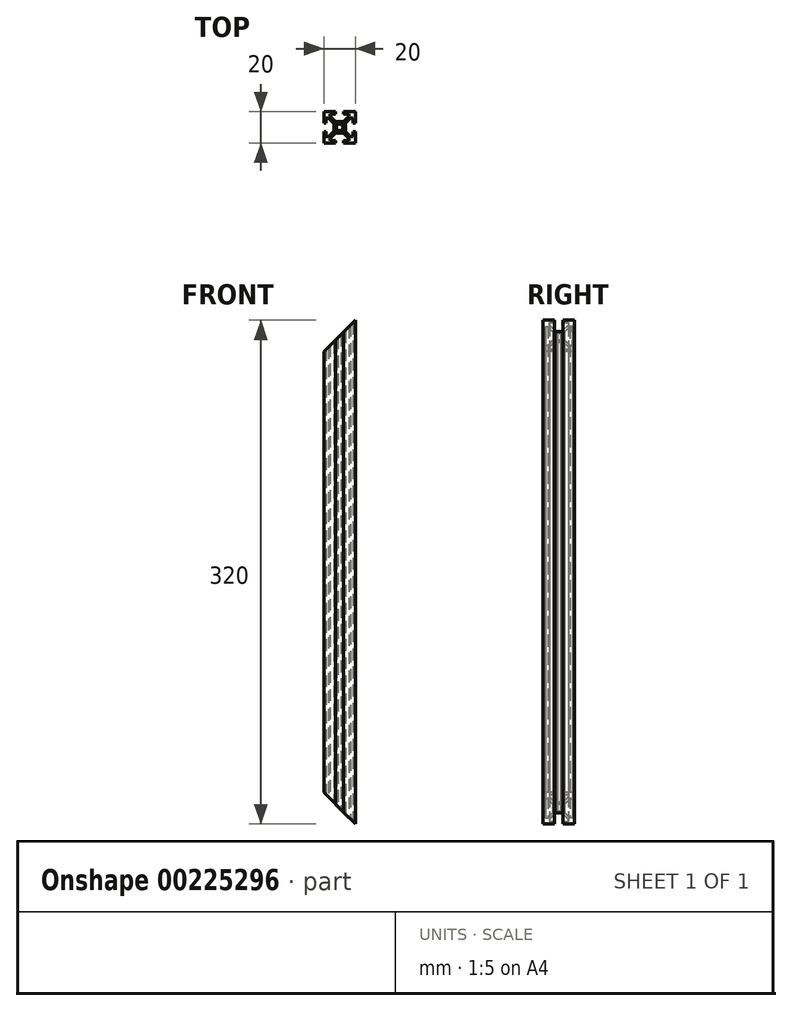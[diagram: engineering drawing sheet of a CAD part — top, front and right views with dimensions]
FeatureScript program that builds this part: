
annotation { "Feature Type Name" : "Feature", "Feature Type Description" : "" }
export const myFeature = defineFeature(function(context is Context, id is Id, definition is map)
    precondition{}
    {
        {
            var Q0;
            Q0=qCreatedBy(makeId("Top.planeOp"),FACE);
            var sketch = newSketch(context, id + "F0", { "sketchPlane" : qUnion([Q0])});
            skLineSegment(sketch, "E0.bottom", {"start": v(10, 10) * mm, "end": v(-10, 10) * mm});
            skLineSegment(sketch, "E0.top", {"start": v(10, -10) * mm, "end": v(-10, -10) * mm});
            skLineSegment(sketch, "E0.left", {"start": v(10, 10) * mm, "end": v(10, -10) * mm});
            skLineSegment(sketch, "E0.right", {"start": v(-10, 10) * mm, "end": v(-10, -10) * mm});
            skPoint(sketch, "E0.middle", {"position": v(0, 0) * mm});
            skLineSegment(sketch, "E1", {"start": v(-10, 10) * mm, "end": v(10, -10) * mm, "construction": true});
            skLineSegment(sketch, "E2", {"start": v(-10, -10) * mm, "end": v(10, 10) * mm, "construction": true});
            skLineSegment(sketch, "E3", {"start": v(0, 10) * mm, "end": v(0, -10) * mm, "construction": true});
            skLineSegment(sketch, "E4", {"start": v(-10, 0) * mm, "end": v(10, 0) * mm, "construction": true});
            skPoint(sketch, "E4.endSnap0", {"position": v(10, 0) * mm});
            skLineSegment(sketch, "E5", {"start": v(-2.63, 13.49) * mm, "end": v(2.63, 13.49) * mm});
            skLineSegment(sketch, "E6", {"start": v(2.63, 13.49) * mm, "end": v(2.63, 8.5) * mm});
            skLineSegment(sketch, "E7", {"start": v(2.63, 8.5) * mm, "end": v(6, 8.5) * mm});
            skLineSegment(sketch, "E8", {"start": v(6, 8.5) * mm, "end": v(6, 7.06) * mm});
            skLineSegment(sketch, "E9", {"start": v(6, 7.06) * mm, "end": v(2.6, 3.66) * mm});
            skLineSegment(sketch, "E10", {"start": v(2.6, 3.66) * mm, "end": v(-2.6, 3.66) * mm});
            skLineSegment(sketch, "E11", {"start": v(-2.6, 3.66) * mm, "end": v(-6, 7.06) * mm});
            skLineSegment(sketch, "E12", {"start": v(-6, 7.06) * mm, "end": v(-6, 8.5) * mm});
            skLineSegment(sketch, "E13", {"start": v(-6, 8.5) * mm, "end": v(-2.63, 8.5) * mm});
            skLineSegment(sketch, "E14", {"start": v(-2.63, 8.5) * mm, "end": v(-2.63, 13.49) * mm});
            skCircle(sketch, "E15", {"center": v(0, 0) * mm, "radius": 2.1 * mm});
            skLineSegment(sketch, "E16.MirrorCS", {"start": v(-7.06, 6) * mm, "end": v(-8.5, 6) * mm});
            skLineSegment(sketch, "E17.MirrorCS", {"start": v(-3.66, 2.6) * mm, "end": v(-7.06, 6) * mm});
            skLineSegment(sketch, "E18.MirrorCS", {"start": v(-8.5, 6) * mm, "end": v(-8.5, 2.63) * mm});
            skLineSegment(sketch, "E19.MirrorCS", {"start": v(-3.66, -2.6) * mm, "end": v(-3.66, 2.6) * mm});
            skLineSegment(sketch, "E20.MirrorCS", {"start": v(-7.06, -6) * mm, "end": v(-3.66, -2.6) * mm});
            skLineSegment(sketch, "E21.MirrorCS", {"start": v(-8.5, -6) * mm, "end": v(-7.06, -6) * mm});
            skLineSegment(sketch, "E22.MirrorCS", {"start": v(-8.5, -2.63) * mm, "end": v(-8.5, -6) * mm});
            skLineSegment(sketch, "E23.MirrorCS", {"start": v(-13.49, -2.63) * mm, "end": v(-8.5, -2.63) * mm});
            skLineSegment(sketch, "E24.MirrorCS", {"start": v(-13.49, 2.63) * mm, "end": v(-13.49, -2.63) * mm});
            skLineSegment(sketch, "E25.MirrorCS", {"start": v(-8.5, 2.63) * mm, "end": v(-13.49, 2.63) * mm});
            skLineSegment(sketch, "E26.MirrorCS", {"start": v(-2.6, -3.66) * mm, "end": v(-6, -7.06) * mm});
            skLineSegment(sketch, "E27.MirrorCS", {"start": v(2.6, -3.66) * mm, "end": v(-2.6, -3.66) * mm});
            skLineSegment(sketch, "E28.MirrorCS", {"start": v(6, -7.06) * mm, "end": v(2.6, -3.66) * mm});
            skLineSegment(sketch, "E29.MirrorCS", {"start": v(6, -8.5) * mm, "end": v(6, -7.06) * mm});
            skLineSegment(sketch, "E30.MirrorCS", {"start": v(2.63, -8.5) * mm, "end": v(6, -8.5) * mm});
            skLineSegment(sketch, "E31.MirrorCS", {"start": v(2.63, -13.49) * mm, "end": v(2.63, -8.5) * mm});
            skLineSegment(sketch, "E32.MirrorCS", {"start": v(-2.63, -13.49) * mm, "end": v(2.63, -13.49) * mm});
            skLineSegment(sketch, "E33.MirrorCS", {"start": v(-2.63, -8.5) * mm, "end": v(-2.63, -13.49) * mm});
            skLineSegment(sketch, "E34.MirrorCS", {"start": v(-6, -8.5) * mm, "end": v(-2.63, -8.5) * mm});
            skLineSegment(sketch, "E35.MirrorCS", {"start": v(-6, -7.06) * mm, "end": v(-6, -8.5) * mm});
            skLineSegment(sketch, "E36.MirrorCS", {"start": v(7.06, 6) * mm, "end": v(3.66, 2.6) * mm});
            skLineSegment(sketch, "E37.MirrorCS", {"start": v(8.5, 6) * mm, "end": v(7.06, 6) * mm});
            skLineSegment(sketch, "E38.MirrorCS", {"start": v(8.5, 2.63) * mm, "end": v(8.5, 6) * mm});
            skLineSegment(sketch, "E39.MirrorCS", {"start": v(13.49, 2.63) * mm, "end": v(8.5, 2.63) * mm});
            skLineSegment(sketch, "E40.MirrorCS", {"start": v(13.49, -2.63) * mm, "end": v(13.49, 2.63) * mm});
            skLineSegment(sketch, "E41.MirrorCS", {"start": v(8.5, -2.63) * mm, "end": v(13.49, -2.63) * mm});
            skLineSegment(sketch, "E42.MirrorCS", {"start": v(8.5, -6) * mm, "end": v(8.5, -2.63) * mm});
            skLineSegment(sketch, "E43.MirrorCS", {"start": v(7.06, -6) * mm, "end": v(8.5, -6) * mm});
            skLineSegment(sketch, "E44.MirrorCS", {"start": v(3.66, -2.6) * mm, "end": v(7.06, -6) * mm});
            skLineSegment(sketch, "E45.MirrorCS", {"start": v(3.66, 2.6) * mm, "end": v(3.66, -2.6) * mm});
            skCircle(sketch, "E46", {"center": v(-1.48, 1.48) * mm, "radius": 0.7 * mm});
            skCircle(sketch, "E47.MirrorC", {"center": v(1.48, 1.48) * mm, "radius": 0.7 * mm});
            skCircle(sketch, "E48.MirrorC", {"center": v(-1.48, -1.48) * mm, "radius": 0.7 * mm});
            skCircle(sketch, "E49.MirrorC", {"center": v(1.48, -1.48) * mm, "radius": 0.7 * mm});
            skSolve(sketch);
        }
        {
            var Q0;
            {var subQ29=sQuery(id+"F0.wireOp",EDGE,"E7");Q0=makeQuery(id+"F0.imprint","IMPRINT",FACE,{"disambiguationData":[TD([[makeQuery(id+"F0.imprint","IMPRINT",EDGE,{"derivedFrom":subQ29}),1.0]])]});}
            extrude(context, id + "F1", {"entities" : qUnion([Q0]), "depth" : 320 * mm});
        }
        {
            var Q0;
            Q0=qCreatedBy(makeId("Front.planeOp"),FACE);
            var sketch = newSketch(context, id + "F2", { "sketchPlane" : qUnion([Q0])});
            skLineSegment(sketch, "E50.0", {"start": v(10, 320) * mm, "end": v(10, 0) * mm});
            skLineSegment(sketch, "E51.0", {"start": v(-10, 320) * mm, "end": v(-10, 0) * mm});
            skLineSegment(sketch, "E52", {"start": v(10, 0) * mm, "end": v(-10, 20) * mm});
            skLineSegment(sketch, "E53.0", {"start": v(10, 0) * mm, "end": v(2.63, 0) * mm});
            skLineSegment(sketch, "E54", {"start": v(-10, 20) * mm, "end": v(-10, 0) * mm});
            skLineSegment(sketch, "E55", {"start": v(10, 0) * mm, "end": v(-10, 0) * mm});
            skLineSegment(sketch, "E56", {"start": v(-91.6, 160) * mm, "end": v(92.38, 160) * mm, "construction": true});
            skLineSegment(sketch, "E57.MirrorCS", {"start": v(10, 320) * mm, "end": v(-10, 300) * mm});
            skLineSegment(sketch, "E58.MirrorCS", {"start": v(-10, 300) * mm, "end": v(-10, 320) * mm});
            skLineSegment(sketch, "E59.MirrorCS", {"start": v(10, 320) * mm, "end": v(-10, 320) * mm});
            skSolve(sketch);
        }
        {
            var Q0;
            Q0=makeQuery(id+"F2.imprint","IMPRINT",FACE,{"disambiguationData":[TD([[makeQuery(id+"F2.imprint","IMPRINT",EDGE,{"derivedFrom":sQuery(id+"F2.wireOp",EDGE,"E57.MirrorCS")}),-1.0]])]});
            var Q1;
            {var subQ0=sQuery(id+"F2.wireOp",EDGE,"E52");Q1=makeQuery(id+"F2.imprint","IMPRINT",FACE,{"disambiguationData":[TD([[makeQuery(id+"F2.imprint","IMPRINT",EDGE,{"derivedFrom":subQ0}),1.0]])]});}
            extrude(context, id + "F3", {"entities" : qUnion([Q0, Q1]), "operationType" : NewBodyOperationType.REMOVE, "endBound" : BoundingType.SYMMETRIC, "oppositeDirection" : true, "depth" : 25.4 * mm});
        }
        {
            var Q0;
            Q0=makeQuery(id+"F3.boolean.opBoolean","COPY",FACE,{"derivedFrom":makeQuery(id+"F3.opExtrude","SWEPT_FACE",FACE,{"disambiguationData":[OSD([sQuery(id+"F2.wireOp",EDGE,"E52")])]})});
            var sketch = newSketch(context, id + "F4", { "sketchPlane" : qUnion([Q0])});
            skLineSegment(sketch, "E60.0", {"start": v(-2.63, 19.1) * mm, "end": v(-2.63, 21.21) * mm});
            skLineSegment(sketch, "E61.0", {"start": v(2.63, 21.21) * mm, "end": v(2.63, 19.1) * mm});
            skLineSegment(sketch, "E62.0", {"start": v(2.63, -4.95) * mm, "end": v(2.63, -7.07) * mm});
            skLineSegment(sketch, "E63.0", {"start": v(-2.63, -7.07) * mm, "end": v(-2.63, -4.95) * mm});
            skLineSegment(sketch, "E64.bottom", {"start": v(-2.63, 21.21) * mm, "end": v(2.63, 21.21) * mm});
            skLineSegment(sketch, "E64.top", {"start": v(-2.63, -7.07) * mm, "end": v(2.63, -7.07) * mm});
            skLineSegment(sketch, "E64.left", {"start": v(-2.63, 21.21) * mm, "end": v(-2.63, -7.07) * mm});
            skLineSegment(sketch, "E64.right", {"start": v(2.63, 21.21) * mm, "end": v(2.63, -7.07) * mm});
            skSolve(sketch);
        }
        {
            var Q0;
            {var subQ0=makeQuery(id+"F3.opExtrude","SWEPT_FACE",FACE,{"disambiguationData":[OSD([sQuery(id+"F2.wireOp",EDGE,"E52")])]});var subQ10=makeQuery(id+"F3.boolean.opBoolean","INTERSECT",EDGE,{"derivedFrom":[makeQuery(id+"F1.opExtrude","SWEPT_FACE",FACE,{"disambiguationData":[OSD([sQuery(id+"F0.wireOp",EDGE,"E19.MirrorCS")])]}),subQ0]});Q0=makeQuery(id+"F4.imprint","IMPRINT",FACE,{"disambiguationData":[TD([[makeQuery(id+"F4.imprint","IMPRINT",EDGE,{"derivedFrom":subQ10}),1.0]])]});}
            extrude(context, id + "F5", {"entities" : qUnion([Q0]), "operationType" : NewBodyOperationType.REMOVE, "oppositeDirection" : true, "depth" : 0.5 * mm});
        }
        {
            var Q0;
            Q0=makeQuery(id+"F3.boolean.opBoolean","COPY",FACE,{"derivedFrom":makeQuery(id+"F3.opExtrude","SWEPT_FACE",FACE,{"disambiguationData":[OSD([sQuery(id+"F2.wireOp",EDGE,"E57.MirrorCS")])]})});
            var sketch = newSketch(context, id + "F6", { "sketchPlane" : qUnion([Q0])});
            skLineSegment(sketch, "E65.0", {"start": v(2.63, 205.06) * mm, "end": v(2.63, 207.18) * mm});
            skLineSegment(sketch, "E66.0", {"start": v(-2.63, 207.18) * mm, "end": v(-2.63, 205.06) * mm});
            skLineSegment(sketch, "E67.0", {"start": v(2.63, 231.22) * mm, "end": v(2.63, 233.35) * mm});
            skLineSegment(sketch, "E68.0", {"start": v(-2.63, 233.35) * mm, "end": v(-2.63, 231.22) * mm});
            skLineSegment(sketch, "E69.bottom", {"start": v(2.63, 205.06) * mm, "end": v(-2.63, 205.06) * mm});
            skLineSegment(sketch, "E69.top", {"start": v(2.63, 233.35) * mm, "end": v(-2.63, 233.35) * mm});
            skLineSegment(sketch, "E69.left", {"start": v(2.63, 205.06) * mm, "end": v(2.63, 233.35) * mm});
            skLineSegment(sketch, "E69.right", {"start": v(-2.63, 205.06) * mm, "end": v(-2.63, 233.35) * mm});
            skSolve(sketch);
        }
        {
            var Q0;
            {var subQ0=makeQuery(id+"F3.opExtrude","SWEPT_FACE",FACE,{"disambiguationData":[OSD([sQuery(id+"F2.wireOp",EDGE,"E57.MirrorCS")])]});var subQ6=makeQuery(id+"F3.boolean.opBoolean","INTERSECT",EDGE,{"derivedFrom":[makeQuery(id+"F1.opExtrude","SWEPT_FACE",FACE,{"disambiguationData":[OSD([sQuery(id+"F0.wireOp",EDGE,"E19.MirrorCS")])]}),subQ0]});Q0=makeQuery(id+"F6.imprint","IMPRINT",FACE,{"disambiguationData":[TD([[makeQuery(id+"F6.imprint","IMPRINT",EDGE,{"derivedFrom":subQ6}),-1.0]])]});}
            extrude(context, id + "F7", {"entities" : qUnion([Q0]), "operationType" : NewBodyOperationType.REMOVE, "oppositeDirection" : true, "depth" : 0.5 * mm});
        }
    });
